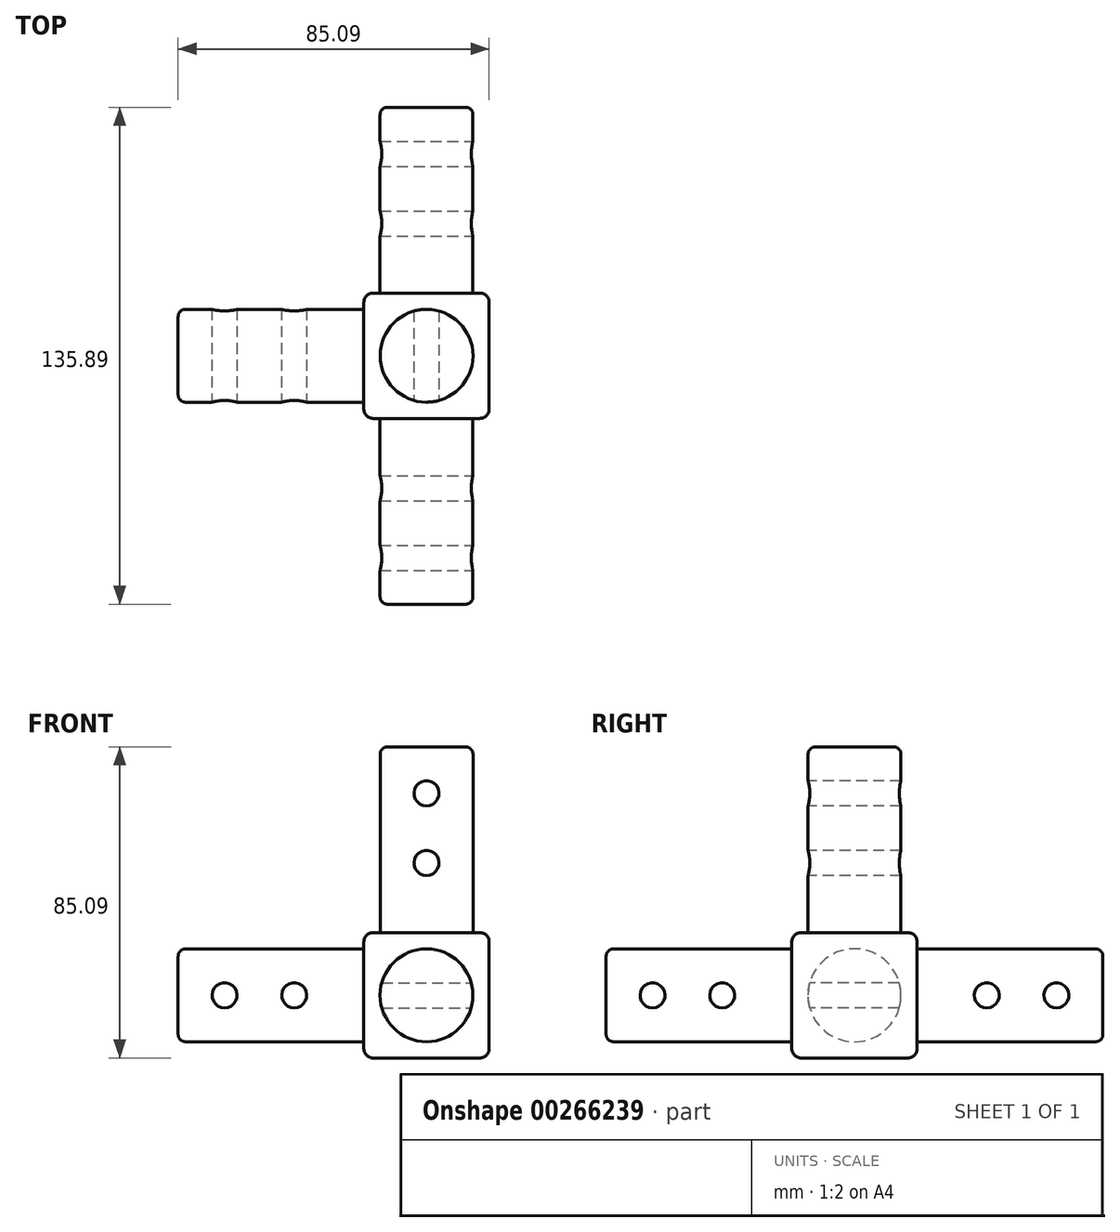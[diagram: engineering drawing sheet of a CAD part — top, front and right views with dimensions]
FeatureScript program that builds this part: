
annotation { "Feature Type Name" : "Feature", "Feature Type Description" : "" }
export const myFeature = defineFeature(function(context is Context, id is Id, definition is map)
    precondition{}
    {
        {
            var Q0;
            Q0=qCreatedBy(makeId("Top.planeOp"),FACE);
            var sketch = newSketch(context, id + "F0", { "sketchPlane" : qUnion([Q0])});
            skLineSegment(sketch, "E0.bottom", {"start": v(-13.47, 23.7) * mm, "end": v(20.82, 23.7) * mm});
            skLineSegment(sketch, "E0.top", {"start": v(-13.47, -10.58) * mm, "end": v(20.82, -10.58) * mm});
            skLineSegment(sketch, "E0.left", {"start": v(-13.47, 23.7) * mm, "end": v(-13.47, -10.58) * mm});
            skLineSegment(sketch, "E0.right", {"start": v(20.82, 23.7) * mm, "end": v(20.82, -10.58) * mm});
            skSolve(sketch);
        }
        {
            var Q0;
            Q0=qSketchRegion(id+"F0",true);
            extrude(context, id + "F1", {"entities" : qUnion([Q0]), "depth" : 34.3 * mm});
        }
        {
            var Q0;
            Q0=makeQuery(id+"F1.opExtrude","CAP_FACE",FACE,{"disambiguationData":[OSD([sQuery(id+"F0.wireOp",EDGE,"E0.bottom"),sQuery(id+"F0.wireOp",EDGE,"E0.top"),sQuery(id+"F0.wireOp",EDGE,"E0.left"),sQuery(id+"F0.wireOp",EDGE,"E0.right")])],"isStart":false});
            var sketch = newSketch(context, id + "F2", { "sketchPlane" : qUnion([Q0])});
            skCircle(sketch, "E1", {"center": v(3.68, 6.56) * mm, "radius": 12.7 * mm});
            skLineSegment(sketch, "E2", {"start": v(3.67, 23.7) * mm, "end": v(3.67, -12.79) * mm, "construction": true});
            skLineSegment(sketch, "E3", {"start": v(20.82, 6.56) * mm, "end": v(-13.47, 6.56) * mm, "construction": true});
            skSolve(sketch);
        }
        {
            var Q0;
            Q0=qSketchRegion(id+"F2",true);
            extrude(context, id + "F3", {"entities" : qUnion([Q0]), "operationType" : NewBodyOperationType.ADD, "depth" : 50.8 * mm});
        }
        {
            var Q0;
            Q0=makeQuery(id+"F1.opExtrude","SWEPT_FACE",FACE,{"disambiguationData":[OSD([sQuery(id+"F0.wireOp",EDGE,"E0.left")])]});
            var sketch = newSketch(context, id + "F4", { "sketchPlane" : qUnion([Q0])});
            skLineSegment(sketch, "E4", {"start": v(-23.7, 17.15) * mm, "end": v(13.45, 17.15) * mm, "construction": true});
            skLineSegment(sketch, "E5", {"start": v(-6.56, 0) * mm, "end": v(-6.56, 34.3) * mm, "construction": true});
            skCircle(sketch, "E6", {"center": v(-6.56, 17.15) * mm, "radius": 12.7 * mm});
            skSolve(sketch);
        }
        {
            var Q0;
            Q0=qSketchRegion(id+"F4",true);
            extrude(context, id + "F5", {"entities" : qUnion([Q0]), "operationType" : NewBodyOperationType.ADD, "depth" : 50.8 * mm});
        }
        {
            var Q0;
            Q0=makeQuery(id+"F1.opExtrude","SWEPT_FACE",FACE,{"disambiguationData":[OSD([sQuery(id+"F0.wireOp",EDGE,"E0.top")])]});
            var sketch = newSketch(context, id + "F6", { "sketchPlane" : qUnion([Q0])});
            skLineSegment(sketch, "E7", {"start": v(-13.47, 17.15) * mm, "end": v(24.43, 17.15) * mm, "construction": true});
            skLineSegment(sketch, "E8", {"start": v(3.67, 0) * mm, "end": v(3.67, 34.3) * mm, "construction": true});
            skCircle(sketch, "E9", {"center": v(3.67, 17.15) * mm, "radius": 12.7 * mm});
            skSolve(sketch);
        }
        {
            var Q0;
            Q0=qSketchRegion(id+"F6",true);
            extrude(context, id + "F7", {"entities" : qUnion([Q0]), "operationType" : NewBodyOperationType.ADD, "depth" : 50.8 * mm});
        }
        {
            var Q0;
            Q0=qCreatedBy(makeId("Front.planeOp"),FACE);
            var sketch = newSketch(context, id + "F8", { "sketchPlane" : qUnion([Q0])});
            skCircle(sketch, "E10", {"center": v(3.67, 53.34) * mm, "radius": 3.43 * mm});
            skCircle(sketch, "E11", {"center": v(3.67, 72.4) * mm, "radius": 3.43 * mm});
            skSolve(sketch);
        }
        {
            var Q0;
            Q0=qSketchRegion(id+"F8",true);
            extrude(context, id + "F9", {"entities" : qUnion([Q0]), "operationType" : NewBodyOperationType.REMOVE, "endBound" : BoundingType.SYMMETRIC, "oppositeDirection" : true, "depth" : 50.8 * mm});
        }
        {
            var Q0;
            Q0=qCreatedBy(makeId("Right.planeOp"),FACE);
            var sketch = newSketch(context, id + "F10", { "sketchPlane" : qUnion([Q0])});
            skCircle(sketch, "E12", {"center": v(-29.63, 17.15) * mm, "radius": 3.43 * mm});
            skCircle(sketch, "E13", {"center": v(-48.68, 17.15) * mm, "radius": 3.43 * mm});
            skSolve(sketch);
        }
        {
            var Q0;
            Q0=qSketchRegion(id+"F10",true);
            extrude(context, id + "F11", {"entities" : qUnion([Q0]), "operationType" : NewBodyOperationType.REMOVE, "endBound" : BoundingType.SYMMETRIC, "oppositeDirection" : true, "depth" : 50.8 * mm});
        }
        {
            var Q0;
            Q0=qCreatedBy(makeId("Front.planeOp"),FACE);
            var sketch = newSketch(context, id + "F12", { "sketchPlane" : qUnion([Q0])});
            skCircle(sketch, "E14", {"center": v(-51.57, 17.15) * mm, "radius": 3.43 * mm});
            skCircle(sketch, "E15", {"center": v(-32.52, 17.15) * mm, "radius": 3.43 * mm});
            skSolve(sketch);
        }
        {
            var Q0;
            Q0=qSketchRegion(id+"F12",true);
            extrude(context, id + "F13", {"entities" : qUnion([Q0]), "operationType" : NewBodyOperationType.REMOVE, "endBound" : BoundingType.SYMMETRIC, "oppositeDirection" : true, "depth" : 50.8 * mm});
        }
        {
            var Q0;
            Q0=makeQuery(id+"F1.opExtrude","SWEPT_EDGE",EDGE,{"disambiguationData":[OSD([sQuery(id+"F0.wireOp",EDGE,"E0.bottom"),sQuery(id+"F0.wireOp",EDGE,"E0.right")])]});
            var Q1;
            Q1=makeQuery(id+"F1.opExtrude","CAP_EDGE",EDGE,{"disambiguationData":[OSD([sQuery(id+"F0.wireOp",EDGE,"E0.right")])],"isStart":false});
            var Q2;
            Q2=makeQuery(id+"F1.opExtrude","SWEPT_EDGE",EDGE,{"disambiguationData":[OSD([sQuery(id+"F0.wireOp",EDGE,"E0.top"),sQuery(id+"F0.wireOp",EDGE,"E0.right")])]});
            var Q3;
            Q3=makeQuery(id+"F1.opExtrude","CAP_EDGE",EDGE,{"disambiguationData":[OSD([sQuery(id+"F0.wireOp",EDGE,"E0.right")])],"isStart":true});
            var Q4;
            Q4=makeQuery(id+"F1.opExtrude","CAP_EDGE",EDGE,{"disambiguationData":[OSD([sQuery(id+"F0.wireOp",EDGE,"E0.bottom")])],"isStart":true});
            var Q5;
            Q5=makeQuery(id+"F1.opExtrude","CAP_EDGE",EDGE,{"disambiguationData":[OSD([sQuery(id+"F0.wireOp",EDGE,"E0.bottom")])],"isStart":false});
            var Q6;
            Q6=makeQuery(id+"F1.opExtrude","SWEPT_EDGE",EDGE,{"disambiguationData":[OSD([sQuery(id+"F0.wireOp",EDGE,"E0.bottom"),sQuery(id+"F0.wireOp",EDGE,"E0.left")])]});
            var Q7;
            Q7=makeQuery(id+"F1.opExtrude","CAP_EDGE",EDGE,{"disambiguationData":[OSD([sQuery(id+"F0.wireOp",EDGE,"E0.left")])],"isStart":true});
            var Q8;
            Q8=makeQuery(id+"F1.opExtrude","CAP_EDGE",EDGE,{"disambiguationData":[OSD([sQuery(id+"F0.wireOp",EDGE,"E0.top")])],"isStart":true});
            var Q9;
            Q9=makeQuery(id+"F1.opExtrude","CAP_EDGE",EDGE,{"disambiguationData":[OSD([sQuery(id+"F0.wireOp",EDGE,"E0.left")])],"isStart":false});
            var Q10;
            Q10=makeQuery(id+"F1.opExtrude","SWEPT_EDGE",EDGE,{"disambiguationData":[OSD([sQuery(id+"F0.wireOp",EDGE,"E0.top"),sQuery(id+"F0.wireOp",EDGE,"E0.left")])]});
            var Q11;
            Q11=makeQuery(id+"F1.opExtrude","CAP_EDGE",EDGE,{"disambiguationData":[OSD([sQuery(id+"F0.wireOp",EDGE,"E0.top")])],"isStart":false});
            fillet(context, id + "F14", {"entities" : qUnion([Q0, Q1, Q2, Q3, Q4, Q5, Q6, Q7, Q8, Q9, Q10, Q11]), "radius" : 2.54 * mm, "tangentPropagation" : true, "allowEdgeOverflow" : false});
        }
        {
            var Q0;
            Q0=makeQuery(id+"F1.opExtrude","SWEPT_FACE",FACE,{"disambiguationData":[OSD([sQuery(id+"F0.wireOp",EDGE,"E0.bottom")])]});
            var sketch = newSketch(context, id + "F15", { "sketchPlane" : qUnion([Q0])});
            skLineSegment(sketch, "E16", {"start": v(-18.28, 17.15) * mm, "end": v(4.82, 17.15) * mm, "construction": true});
            skPoint(sketch, "E16.endSnap0", {"position": v(-18.28, 17.15) * mm});
            skLineSegment(sketch, "E17", {"start": v(-3.67, 31.75) * mm, "end": v(-3.67, 14.65) * mm, "construction": true});
            skCircle(sketch, "E18", {"center": v(-3.67, 17.15) * mm, "radius": 12.7 * mm});
            skSolve(sketch);
        }
        {
            var Q0;
            Q0=qSketchRegion(id+"F15",true);
            extrude(context, id + "F16", {"entities" : qUnion([Q0]), "operationType" : NewBodyOperationType.ADD, "depth" : 50.8 * mm});
        }
        {
            var Q0;
            Q0=qCreatedBy(makeId("Right.planeOp"),FACE);
            var sketch = newSketch(context, id + "F17", { "sketchPlane" : qUnion([Q0])});
            skCircle(sketch, "E19", {"center": v(42.76, 17.15) * mm, "radius": 3.43 * mm});
            skCircle(sketch, "E20", {"center": v(61.8, 17.15) * mm, "radius": 3.43 * mm});
            skSolve(sketch);
        }
        {
            var Q0;
            Q0=qSketchRegion(id+"F17",true);
            extrude(context, id + "F18", {"entities" : qUnion([Q0]), "operationType" : NewBodyOperationType.REMOVE, "endBound" : BoundingType.SYMMETRIC, "oppositeDirection" : true, "depth" : 50.8 * mm});
        }
        {
            var Q0;
            Q0=makeQuery(id+"F3.opExtrude","CAP_EDGE",EDGE,{"disambiguationData":[OSD([sQuery(id+"F2.wireOp",EDGE,"E1")])],"isStart":false});
            var Q1;
            Q1=makeQuery(id+"F7.opExtrude","CAP_EDGE",EDGE,{"disambiguationData":[OSD([sQuery(id+"F6.wireOp",EDGE,"E9")])],"isStart":false});
            var Q2;
            Q2=makeQuery(id+"F5.opExtrude","CAP_EDGE",EDGE,{"disambiguationData":[OSD([sQuery(id+"F4.wireOp",EDGE,"E6")])],"isStart":false});
            var Q3;
            Q3=makeQuery(id+"F16.opExtrude","CAP_EDGE",EDGE,{"disambiguationData":[OSD([sQuery(id+"F15.wireOp",EDGE,"E18")])],"isStart":false});
            fillet(context, id + "F19", {"entities" : qUnion([Q0, Q1, Q2, Q3]), "radius" : 2.03 * mm, "tangentPropagation" : true, "allowEdgeOverflow" : false});
        }
    });
